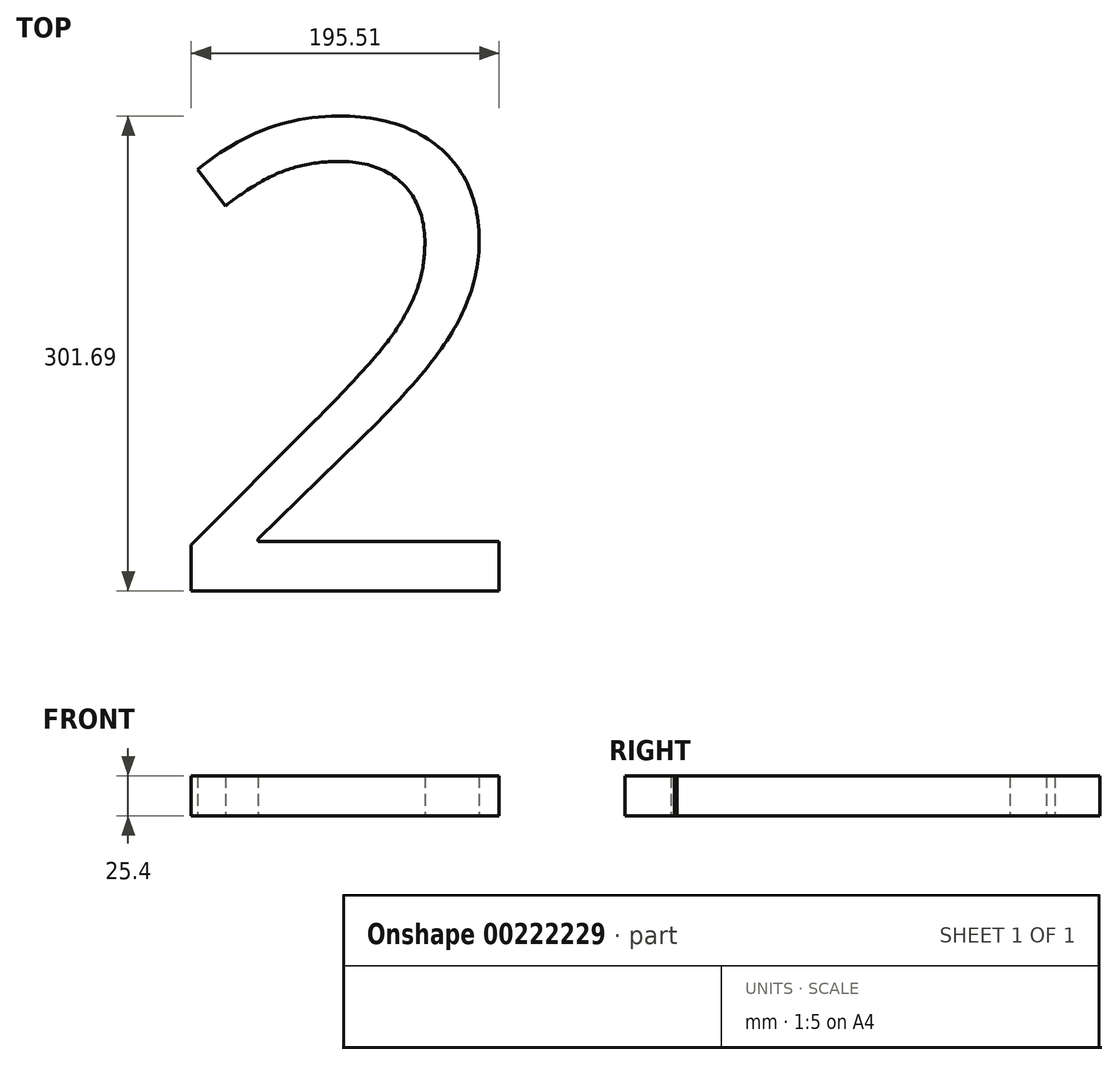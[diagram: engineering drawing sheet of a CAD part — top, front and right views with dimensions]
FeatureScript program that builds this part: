
annotation { "Feature Type Name" : "Feature", "Feature Type Description" : "" }
export const myFeature = defineFeature(function(context is Context, id is Id, definition is map)
    precondition{}
    {
        {
            var Q0;
            Q0=qCreatedBy(makeId("Top.planeOp"),FACE);
            var sketch = newSketch(context, id + "F0", { "sketchPlane" : qUnion([Q0])});
            skText(sketch, "E0", { "text": "2", "fontName": "OpenSans-Regular.ttf"});
            const initialGuessF0  = {"E0": [0, 0, 1, 0, 0.3]};
            skSetInitialGuess(sketch, initialGuessF0);
            skSolve(sketch);
        }
        {
            var Q0;
            Q0 = qSketchRegion(id + "F0", true);
            extrude(context, id + "F1", {"entities" : qUnion([Q0]), "depth" : 25.4 * mm});
        }
    });
